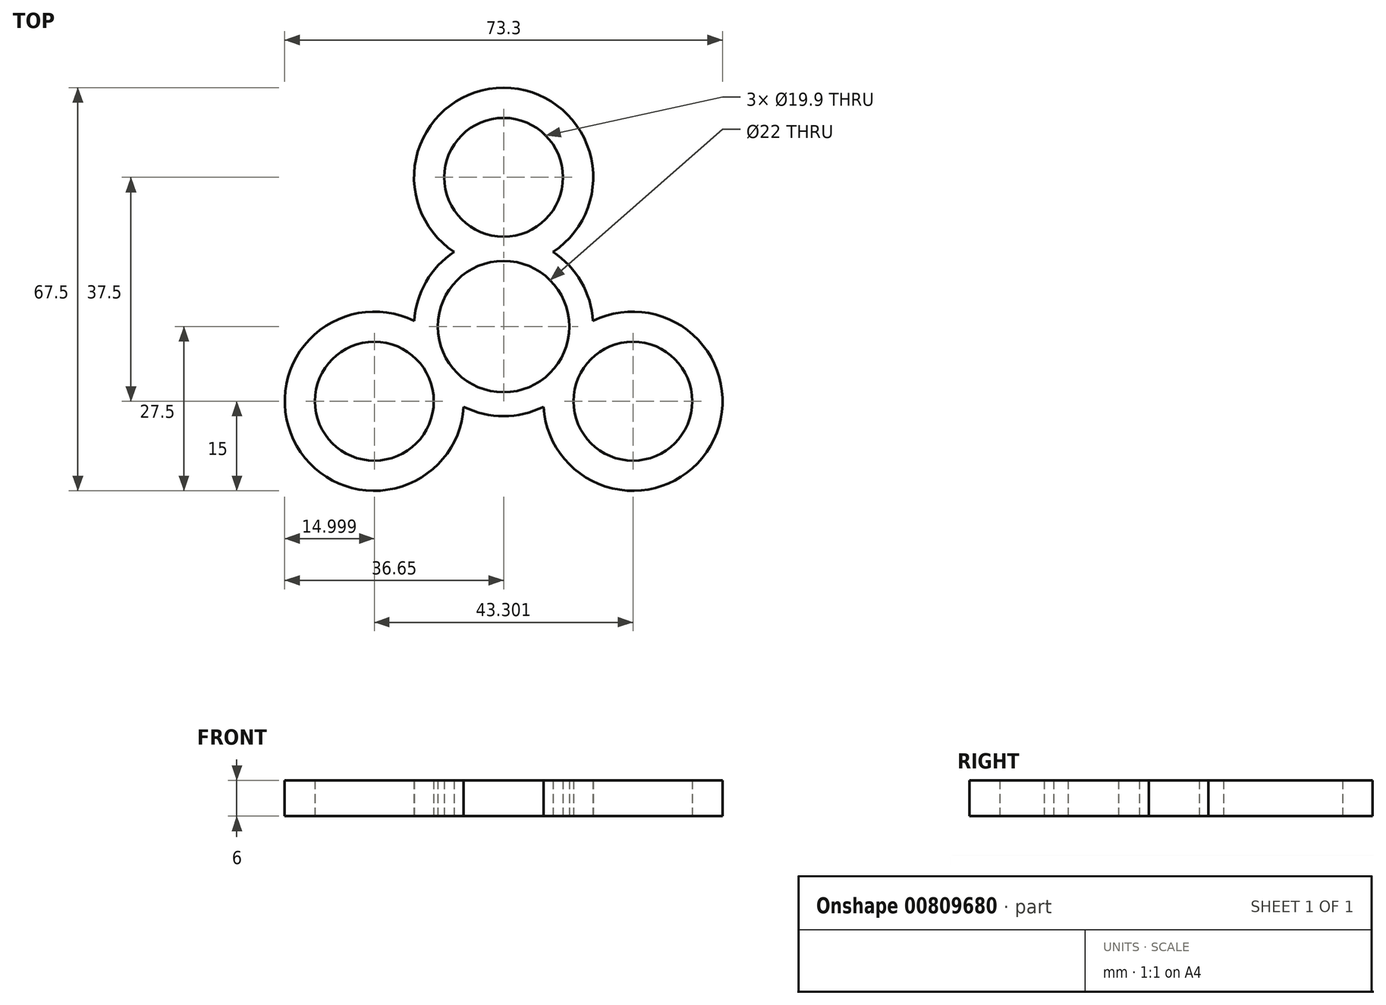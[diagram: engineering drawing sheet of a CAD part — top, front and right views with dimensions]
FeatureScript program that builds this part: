
annotation { "Feature Type Name" : "Feature", "Feature Type Description" : "" }
export const myFeature = defineFeature(function(context is Context, id is Id, definition is map)
    precondition{}
    {
        {
            var Q0;
            Q0=qCreatedBy(makeId("Top.planeOp"),FACE);
            var sketch = newSketch(context, id + "F0", { "sketchPlane" : qUnion([Q0])});
            skArc(sketch, "E0", {"start": v(9.53, 5.5) * mm, "mid": v(0, 11) * mm, "end": v(-9.53, 5.5) * mm});
            skCircle(sketch, "E1", {"center": v(0, 25) * mm, "radius": 9.95 * mm});
            skArc(sketch, "E2", {"start": v(-8.3, 12.5) * mm, "mid": v(-10.93, 10.27) * mm, "end": v(-13, 7.5) * mm});
            skArc(sketch, "E3", {"start": v(8.3, 12.5) * mm, "mid": v(0, 40) * mm, "end": v(-8.3, 12.5) * mm});
            skArc(sketch, "E4.trimOffspring", {"start": v(13, 7.5) * mm, "mid": v(10.93, 10.27) * mm, "end": v(8.3, 12.5) * mm});
            skArc(sketch, "E5.1.0", {"start": v(-13, 7.5) * mm, "mid": v(-14.36, 4.33) * mm, "end": v(-14.97, 0.93) * mm});
            skArc(sketch, "E5.1.1", {"start": v(-6.68, -13.43) * mm, "mid": v(-3.43, -14.6) * mm, "end": v(0, -15) * mm});
            skArc(sketch, "E5.1.2", {"start": v(-9.53, 5.5) * mm, "mid": v(-9.53, -5.5) * mm, "end": v(0, -11) * mm});
            skCircle(sketch, "E5.1.3", {"center": v(-21.65, -12.5) * mm, "radius": 9.95 * mm});
            skArc(sketch, "E5.1.4", {"start": v(-14.97, 0.93) * mm, "mid": v(-34.64, -20) * mm, "end": v(-6.68, -13.43) * mm});
            skArc(sketch, "E5.2.0", {"start": v(0, -15) * mm, "mid": v(3.43, -14.6) * mm, "end": v(6.68, -13.43) * mm});
            skArc(sketch, "E5.2.1", {"start": v(14.97, 0.93) * mm, "mid": v(14.36, 4.33) * mm, "end": v(13, 7.5) * mm});
            skArc(sketch, "E5.2.2", {"start": v(0, -11) * mm, "mid": v(9.53, -5.5) * mm, "end": v(9.53, 5.5) * mm});
            skCircle(sketch, "E5.2.3", {"center": v(21.65, -12.5) * mm, "radius": 9.95 * mm});
            skArc(sketch, "E5.2.4", {"start": v(6.68, -13.43) * mm, "mid": v(34.64, -20) * mm, "end": v(14.97, 0.93) * mm});
            skSolve(sketch);
        }
        {
            var Q0;
            Q0=makeQuery(id+"F0.imprint","IMPRINT",FACE,{"disambiguationData":[TD([[makeQuery(id+"F0.imprint","IMPRINT",EDGE,{"derivedFrom":sQuery(id+"F0.wireOp",EDGE,"E0")}),-1.0]])]});
            extrude(context, id + "F1", {"entities" : qUnion([Q0]), "depth" : 6 * mm, "offsetDistance" : 25 * mm});
        }
    });
